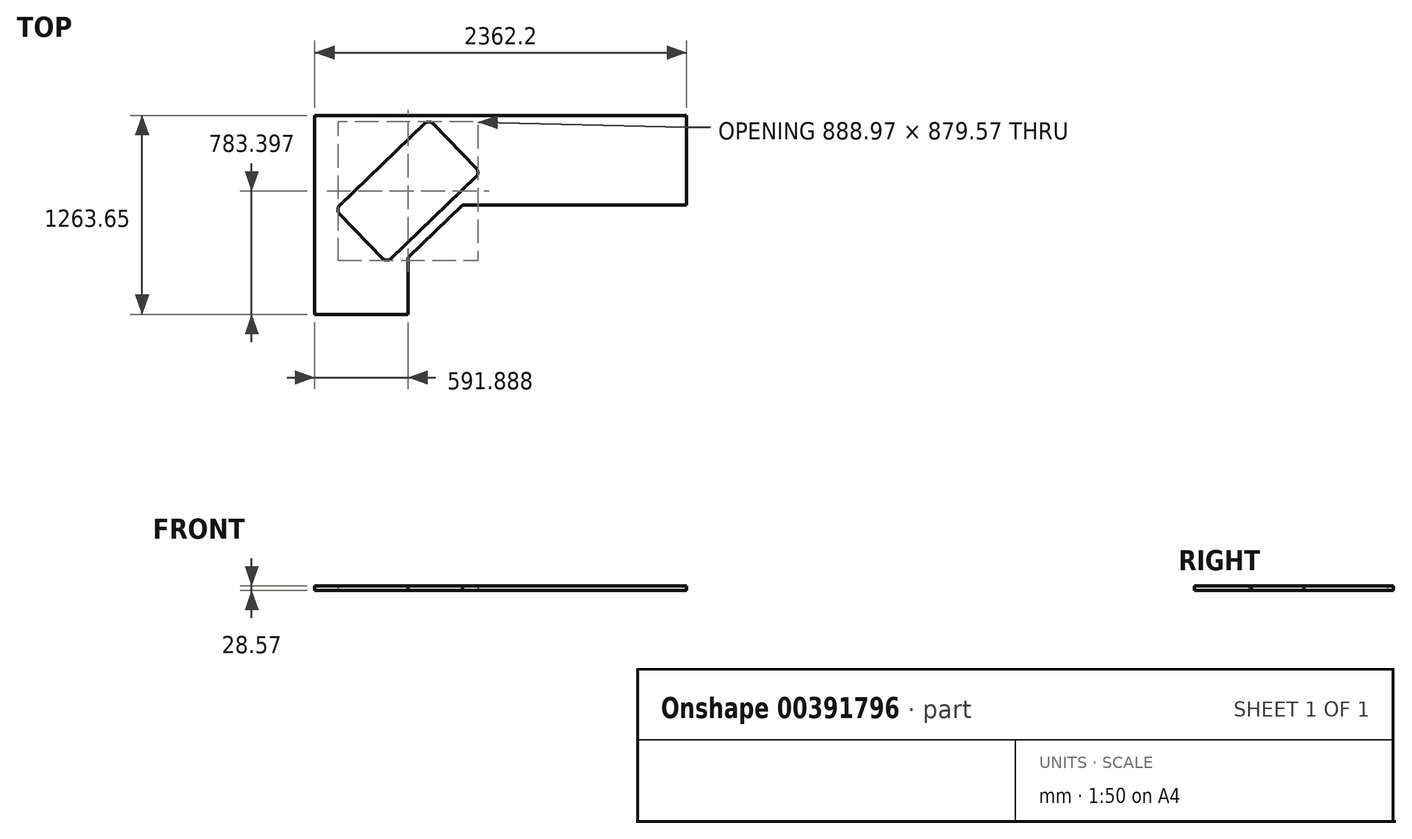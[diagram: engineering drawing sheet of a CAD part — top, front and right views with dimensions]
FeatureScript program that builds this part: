
annotation { "Feature Type Name" : "Feature", "Feature Type Description" : "" }
export const myFeature = defineFeature(function(context is Context, id is Id, definition is map)
    precondition{}
    {
        {
            var Q0;
            Q0=qCreatedBy(makeId("Top.planeOp"),FACE);
            var sketch = newSketch(context, id + "F0", { "sketchPlane" : qUnion([Q0])});
            skLineSegment(sketch, "E0.top", {"start": v(0, -1263.65) * mm, "end": v(593.73, -1263.65) * mm});
            skLineSegment(sketch, "E0.right", {"start": v(593.73, -901.7) * mm, "end": v(593.73, -1263.65) * mm});
            skLineSegment(sketch, "E1.top", {"start": v(939.8, -568.33) * mm, "end": v(2362.2, -568.33) * mm});
            skLineSegment(sketch, "E1.right", {"start": v(2362.2, 0) * mm, "end": v(2362.2, -568.33) * mm});
            skLineSegment(sketch, "E2", {"start": v(0, 0) * mm, "end": v(2362.2, 0) * mm});
            skLineSegment(sketch, "E3", {"start": v(0, 0) * mm, "end": v(0, -1263.65) * mm});
            skLineSegment(sketch, "E4", {"start": v(593.73, -901.7) * mm, "end": v(939.8, -568.33) * mm});
            skLineSegment(sketch, "E5", {"start": v(485.07, -909.38) * mm, "end": v(1024.71, -389.54) * mm});
            skLineSegment(sketch, "E6", {"start": v(1025.72, -335.67) * mm, "end": v(752.58, -52.13) * mm});
            skLineSegment(sketch, "E7", {"start": v(698.7, -51.12) * mm, "end": v(159.06, -570.96) * mm});
            skLineSegment(sketch, "E8", {"start": v(158.06, -624.83) * mm, "end": v(431.2, -908.38) * mm});
            skPoint(sketch, "E9", {"position": v(766.76, -735.01) * mm});
            skPoint(sketch, "E10", {"position": v(754.89, -649.46) * mm});
            skLineSegment(sketch, "E11", {"start": v(766.76, -735.01) * mm, "end": v(718.3, -684.7) * mm, "construction": true});
            skPoint(sketch, "E12.visualSharp", {"position": v(131.63, -597.4) * mm});
            skArc(sketch, "E12.filletArc", {"start": v(159.06, -570.96) * mm, "mid": v(147.4, -597.7) * mm, "end": v(158.06, -624.83) * mm});
            skPoint(sketch, "E13.visualSharp", {"position": v(457.63, -935.82) * mm});
            skArc(sketch, "E13.filletArc", {"start": v(431.2, -908.38) * mm, "mid": v(457.92, -920.04) * mm, "end": v(485.07, -909.38) * mm});
            skPoint(sketch, "E14.visualSharp", {"position": v(726.15, -24.69) * mm});
            skArc(sketch, "E14.filletArc", {"start": v(752.58, -52.13) * mm, "mid": v(725.85, -40.47) * mm, "end": v(698.7, -51.12) * mm});
            skPoint(sketch, "E15.visualSharp", {"position": v(1052.15, -363.11) * mm});
            skArc(sketch, "E15.filletArc", {"start": v(1024.71, -389.54) * mm, "mid": v(1036.37, -362.82) * mm, "end": v(1025.72, -335.67) * mm});
            skLineSegment(sketch, "E16", {"start": v(939.8, -568.33) * mm, "end": v(891.34, -518.02) * mm});
            skLineSegment(sketch, "E17", {"start": v(593.73, -901.7) * mm, "end": v(545.27, -851.4) * mm});
            skLineSegment(sketch, "E18", {"start": v(724.43, -40.47) * mm, "end": v(724.43, 0) * mm});
            skPoint(sketch, "E18.startSnap0", {"position": v(725.85, -40.47) * mm});
            skSolve(sketch);
        }
        {
            var Q0;
            Q0 = qSketchRegion(id + "F0", true);
            extrude(context, id + "F1", {"entities" : qUnion([Q0]), "depth" : 28.57 * mm});
        }
    });
